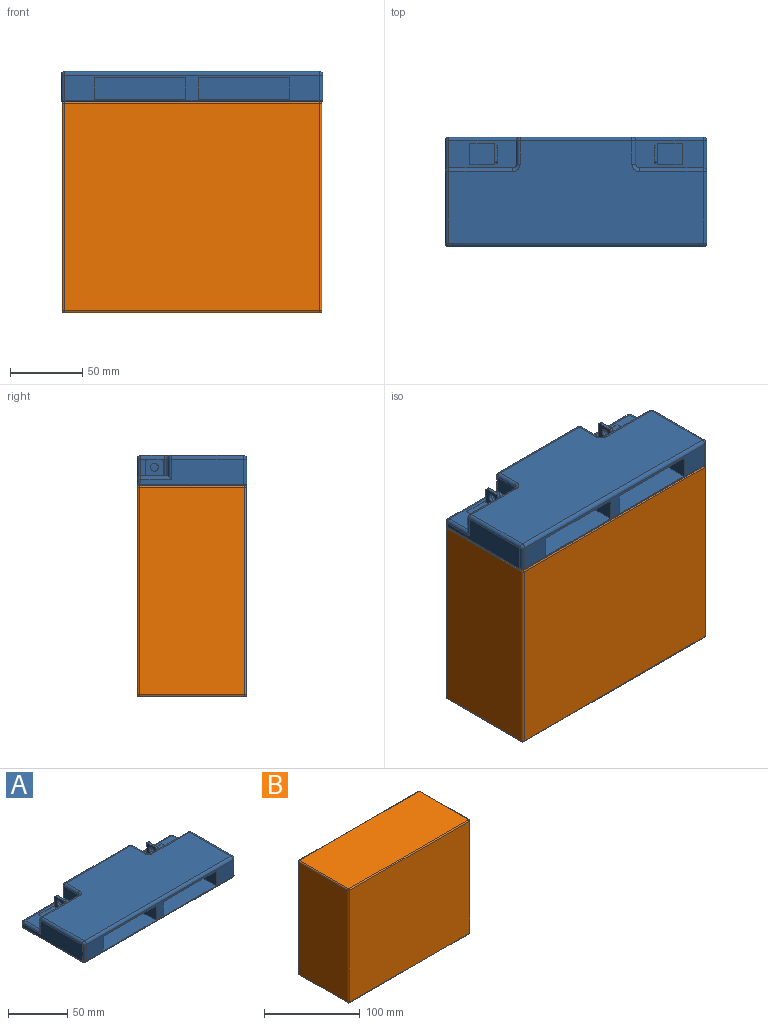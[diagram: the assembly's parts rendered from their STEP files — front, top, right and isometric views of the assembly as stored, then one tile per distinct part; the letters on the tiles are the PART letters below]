
ASSEMBLY  parts=2 mates=1
PART A: 104 faces, bbox 181.1x76x21.1 mm
  f0: plane 14.62x11.76mm, normal (-1,0,0), area 117.3mm2, adj f3,f4,f6,f7,f8,f9,f10,f61
  f1: plane 14.62x11.76mm, normal (1,0,0), area 117.3mm2, adj f11,f12,f13,f14,f21,f22,f65,f66
  f2: plane 179.61x74.45mm, normal (0,0,-1), area 13359mm2, adj f24,f25,f26,f27,f28,f29,f30,f31
  f3: cylinder r=1.27mm len=2.01mm, axis (1,0,0), area 4mm2, adj f0,f4,f5,f9
  f4: plane 9.45x2.01mm, normal (0,0,1), area 19mm2, adj f0,f3,f5,f6
  f5: plane 11.99x11.51mm, normal (1,0,0), area 113.6mm2, adj f3,f4,f6,f7,f8,f9,f10
  f6: cylinder r=1.27mm len=2.01mm, axis (1,0,0), area 4mm2, adj f0,f4,f5,f8
  f7: cylinder r=2.74mm len=5.49mm, axis (1,0,0), area 34.6mm2, adj f0,f5
  f8: plane 10.24x2.01mm, normal (0,1,0), area 20.5mm2, adj f0,f5,f6,f10
  f9: plane 10.24x2.01mm, normal (0,-1,0), area 20.5mm2, adj f0,f3,f5,f10
  f10: plane 46.74x18.8mm, normal (0,0,1), area 601.2mm2, adj f0,f5,f8,f9,f19,f60,f61,f62
  f11: cylinder r=1.27mm len=2.01mm, axis (-1,0,0), area 4mm2, adj f1,f12,f22,f23
  f12: plane 9.45x2.01mm, normal (0,0,1), area 19mm2, adj f1,f11,f13,f23
  f13: cylinder r=1.27mm len=2.01mm, axis (-1,0,0), area 4mm2, adj f1,f12,f21,f23
  f14: cylinder r=2.74mm len=5.49mm, axis (1,0,0), area 34.6mm2, adj f1,f23
  f15: plane 19.05x14.4mm, normal (-1,0,0), area 274.3mm2, adj f44,f45,f46,f71
  f16: plane 19.05x14.4mm, normal (1,0,0), area 274.3mm2, adj f44,f45,f46,f71
  f17: plane 19.05x14.4mm, normal (-1,0,0), area 274.3mm2, adj f47,f48,f49,f71
  f18: plane 19.05x14.4mm, normal (1,0,0), area 274.3mm2, adj f47,f48,f49,f71
  f19: plane 16.26x11.68mm, normal (-1,0,0), area 189.9mm2, adj f10,f86,f95,f96
  f20: plane 16.26x11.68mm, normal (1,0,0), area 189.9mm2, adj f79,f99,f101,f103
  f21: plane 10.24x2.01mm, normal (0,1,0), area 20.5mm2, adj f1,f13,f23,f99
  f22: plane 10.24x2.01mm, normal (0,-1,0), area 20.5mm2, adj f1,f11,f23,f99
  f23: plane 11.99x11.51mm, normal (-1,0,0), area 113.6mm2, adj f11,f12,f13,f14,f21,f22,f99
  f24: cylinder r=1.27mm len=174.5mm, axis (-1,0,0), area 256.9mm2, adj f2,f25,f26,f43
  f25: bspline ~1.22x0.92mm, area 1.3mm2, adj f2,f24,f27,f43
  f26: bspline ~1.22x0.92mm, area 1.3mm2, adj f2,f24,f28,f43
  f27: bspline ~2.54x2.54mm, area 5.7mm2, adj f2,f25,f29,f98
  f28: bspline ~2.54x2.54mm, area 5.7mm2, adj f2,f26,f30,f42
  f29: bspline ~1.22x0.92mm, area 1.3mm2, adj f2,f27,f31,f73
  f30: bspline ~1.22x0.92mm, area 1.3mm2, adj f2,f28,f32,f41
  f31: cylinder r=1.27mm len=69.34mm, axis (0,-1,0), area 102.1mm2, adj f2,f29,f33,f73
  f32: cylinder r=1.27mm len=69.34mm, axis (0,1,0), area 102.1mm2, adj f2,f30,f34,f41
  f33: bspline ~1.22x0.92mm, area 1.3mm2, adj f2,f31,f35,f73
  f34: bspline ~1.22x0.92mm, area 1.3mm2, adj f2,f32,f36,f41
  f35: bspline ~2.54x2.54mm, area 5.7mm2, adj f2,f33,f37,f72
  f36: bspline ~2.54x2.54mm, area 5.7mm2, adj f2,f34,f38,f40
  f37: bspline ~1.22x0.92mm, area 1.3mm2, adj f2,f35,f39,f71
  f38: bspline ~1.22x0.92mm, area 1.3mm2, adj f2,f36,f39,f71
  f39: cylinder r=1.27mm len=174.5mm, axis (1,0,0), area 256.9mm2, adj f2,f37,f38,f71
  f40: cylinder r=2.54mm len=3.1mm, axis (0,0,1), area 12.4mm2, adj f36,f41,f71,f76
  f41: plane 70.87x17.38mm, normal (-1,0,0), area 928mm2, adj f30,f32,f34,f40,f42,f74,f82,f93
  f42: cylinder r=2.54mm len=17.33mm, axis (0,0,1), area 69.1mm2, adj f28,f41,f43,f83
  f43: plane 176.02x17.38mm, normal (0,-1,0), area 1128.3mm2, adj f24,f25,f26,f42,f50,f51,f52,f53
  f44: plane 33.02x19.05mm, normal (0,0,1), area 629mm2, adj f15,f16,f46,f71
  f45: plane 33.02x19.05mm, normal (0,0,-1), area 629mm2, adj f15,f16,f46,f71
  f46: plane 33.02x14.4mm, normal (0,1,0), area 475.5mm2, adj f15,f16,f44,f45
  f47: plane 33.02x19.05mm, normal (0,0,1), area 629mm2, adj f17,f18,f49,f71
  f48: plane 33.02x19.05mm, normal (0,0,-1), area 629mm2, adj f17,f18,f49,f71
  f49: plane 33.02x14.4mm, normal (0,1,0), area 475.5mm2, adj f17,f18,f47,f48
  f50: plane 19.56x15.2mm, normal (1,0,0), area 297.3mm2, adj f43,f51,f53,f54
  f51: plane 63.5x19.56mm, normal (0,0,1), area 1241.9mm2, adj f43,f50,f52,f54
  f52: plane 19.56x15.2mm, normal (-1,0,0), area 297.3mm2, adj f43,f51,f53,f54
  f53: plane 63.5x19.56mm, normal (0,0,-1), area 1241.9mm2, adj f43,f50,f52,f54
  f54: plane 63.5x15.2mm, normal (0,-1,0), area 965.3mm2, adj f50,f51,f52,f53
  f55: plane 19.56x15.2mm, normal (1,0,0), area 297.3mm2, adj f43,f56,f58,f59
  f56: plane 63.5x19.56mm, normal (0,0,1), area 1241.9mm2, adj f43,f55,f57,f59
  f57: plane 19.56x15.2mm, normal (-1,0,0), area 297.3mm2, adj f43,f56,f58,f59
  f58: plane 63.5x19.56mm, normal (0,0,-1), area 1241.9mm2, adj f43,f55,f57,f59
  f59: plane 63.5x15.2mm, normal (0,-1,0), area 965.3mm2, adj f55,f56,f57,f58
  f60: plane 14.62x0.25mm, normal (1,0,0), area 3.7mm2, adj f10,f61,f62,f63
  f61: plane 17.22x0.25mm, normal (0,-1,0), area 4.4mm2, adj f0,f10,f60,f63
  f62: plane 17.22x0.25mm, normal (0,1,0), area 4.4mm2, adj f0,f10,f60,f63
  f63: plane 17.22x14.62mm, normal (0,0,1), area 251.8mm2, adj f0,f60,f61,f62
  f64: plane 14.62x0.25mm, normal (-1,0,0), area 3.7mm2, adj f65,f66,f67,f99
  f65: plane 17.22x0.25mm, normal (0,-1,0), area 4.4mm2, adj f1,f64,f67,f99
  f66: plane 17.22x0.25mm, normal (0,1,0), area 4.4mm2, adj f1,f64,f67,f99
  f67: plane 17.22x14.62mm, normal (0,0,1), area 251.8mm2, adj f1,f64,f65,f66
  f68: cylinder r=2.54mm len=49.28mm, axis (-1,0,0), area 191.5mm2, adj f70,f71,f99,f103
  f69: cylinder r=2.54mm len=21.34mm, axis (0,1,0), area 80.1mm2, adj f70,f73,f99,f100
  f70: sphere r=2.54mm, area 6.5mm2, adj f68,f69,f72
  f71: plane 176.02x17.38mm, normal (0,1,0), area 706.1mm2, adj f15,f16,f17,f18,f37,f38,f39,f40
  f72: cylinder r=2.54mm len=3.1mm, axis (0,0,1), area 12.4mm2, adj f35,f70,f71,f73
  f73: plane 70.87x17.38mm, normal (1,0,0), area 928mm2, adj f29,f31,f33,f69,f72,f80,f98,f100
  f74: cylinder r=2.54mm len=21.34mm, axis (0,-1,0), area 80.1mm2, adj f10,f41,f76,f93
  f75: cylinder r=2.54mm len=49.28mm, axis (-1,0,0), area 191.5mm2, adj f10,f71,f76,f96
  f76: sphere r=2.54mm, area 13.8mm2, adj f40,f74,f75
  f77: cylinder r=2.54mm len=44.2mm, axis (-1,0,0), area 176.3mm2, adj f78,f89,f97,f102
  f78: torus R=5.08mm, axis (0,0,1), area 21.7mm2, adj f77,f79,f97,f101
  f79: cylinder r=2.54mm len=16.26mm, axis (0,1,0), area 64.9mm2, adj f20,f78,f92,f97
  f80: cylinder r=2.54mm len=49.53mm, axis (0,-1,0), area 197.6mm2, adj f73,f88,f89,f97
  f81: cylinder r=2.54mm len=176.02mm, axis (-1,0,0), area 702.3mm2, adj f43,f83,f88,f97
  f82: cylinder r=2.54mm len=49.53mm, axis (0,1,0), area 197.6mm2, adj f41,f83,f87,f97
  f83: sphere r=2.54mm, area 10.1mm2, adj f42,f81,f82
  f84: cylinder r=2.54mm len=44.2mm, axis (-1,0,0), area 176.3mm2, adj f85,f87,f94,f97
  f85: torus R=5.08mm, axis (0,0,1), area 21.7mm2, adj f84,f86,f95,f97
  f86: cylinder r=2.54mm len=16.26mm, axis (0,-1,0), area 64.9mm2, adj f19,f85,f91,f97
  f87: sphere r=2.54mm, area 13.8mm2, adj f82,f84,f93
  f88: sphere r=2.54mm, area 10.1mm2, adj f80,f81,f98
  f89: sphere r=2.54mm, area 6.5mm2, adj f77,f80,f100
  f90: cylinder r=2.54mm len=77.47mm, axis (1,0,0), area 309.1mm2, adj f71,f91,f92,f97
  f91: sphere r=2.54mm, area 13.8mm2, adj f86,f90,f96
  f92: sphere r=2.54mm, area 6.5mm2, adj f79,f90,f103
  f93: cylinder r=2.54mm len=14.22mm, axis (0,0,-1), area 51.7mm2, adj f41,f74,f87,f94
  f94: plane 44.2x11.68mm, normal (0,1,0), area 516.4mm2, adj f10,f84,f93,f95
  f95: cylinder r=2.54mm len=11.68mm, axis (0,0,-1), area 46.6mm2, adj f10,f19,f85,f94
  f96: cylinder r=2.54mm len=14.22mm, axis (0,0,1), area 51.7mm2, adj f19,f71,f75,f91
  f97: plane 176.02x70.87mm, normal (0,0,1), area 10382.3mm2, adj f77,f78,f79,f80,f81,f82,f84,f85
  f98: cylinder r=2.54mm len=17.33mm, axis (0,0,1), area 69.1mm2, adj f27,f43,f73,f88
  f99: plane 46.74x18.8mm, normal (0,0,1), area 601.2mm2, adj f1,f20,f21,f22,f23,f64,f65,f66
  f100: cylinder r=2.54mm len=14.22mm, axis (0,0,1), area 51.7mm2, adj f69,f73,f89,f102
  f101: cylinder r=2.54mm len=11.68mm, axis (0,0,-1), area 46.6mm2, adj f20,f78,f99,f102
  f102: plane 44.2x11.68mm, normal (0,1,0), area 516.4mm2, adj f77,f99,f100,f101
  f103: cylinder r=2.54mm len=14.22mm, axis (0,0,-1), area 51.7mm2, adj f20,f68,f71,f92
PART B: 26 faces, bbox 179.6x75.4x145.8 mm
  f0: sphere r=1.27mm, area 2.5mm2, adj f3,f18,f19
  f1: sphere r=1.27mm, area 2.5mm2, adj f6,f9,f19
  f2: sphere r=1.27mm, area 2.5mm2, adj f3,f7,f16
  f3: cylinder r=1.27mm len=143.26mm, axis (0,0,1), area 285.8mm2, adj f0,f2,f20,f24
  f4: sphere r=1.27mm, area 2.5mm2, adj f11,f17,f18
  f5: sphere r=1.27mm, area 2.5mm2, adj f6,f7,f14
  f6: cylinder r=1.27mm len=143.26mm, axis (0,0,1), area 285.8mm2, adj f1,f5,f20,f21
  f7: cylinder r=1.27mm len=72.9mm, axis (0,1,0), area 145.4mm2, adj f2,f5,f20,f22
  f8: sphere r=1.27mm, area 2.5mm2, adj f9,f13,f17
  f9: cylinder r=1.27mm len=177.04mm, axis (1,0,0), area 353.2mm2, adj f1,f8,f21,f23
  f10: sphere r=1.27mm, area 2.5mm2, adj f11,f15,f16
  f11: cylinder r=1.27mm len=143.26mm, axis (0,0,1), area 285.8mm2, adj f4,f10,f24,f25
  f12: sphere r=1.27mm, area 2.5mm2, adj f13,f14,f15
  f13: cylinder r=1.27mm len=143.26mm, axis (0,0,1), area 285.8mm2, adj f8,f12,f21,f25
  f14: cylinder r=1.27mm len=177.04mm, axis (1,0,0), area 353.2mm2, adj f5,f12,f21,f22
  f15: cylinder r=1.27mm len=72.9mm, axis (0,-1,0), area 145.4mm2, adj f10,f12,f22,f25
  f16: cylinder r=1.27mm len=177.04mm, axis (-1,0,0), area 353.2mm2, adj f2,f10,f22,f24
  f17: cylinder r=1.27mm len=72.9mm, axis (0,-1,0), area 145.4mm2, adj f4,f8,f23,f25
  f18: cylinder r=1.27mm len=177.04mm, axis (-1,0,0), area 353.2mm2, adj f0,f4,f23,f24
  f19: cylinder r=1.27mm len=72.9mm, axis (0,1,0), area 145.4mm2, adj f0,f1,f20,f23
  f20: plane 143.26x72.9mm, normal (-1,0,0), area 10443.1mm2, adj f3,f6,f7,f19
  f21: plane 177.04x143.26mm, normal (0,1,0), area 25361.8mm2, adj f6,f9,f13,f14
  f22: plane 177.04x72.9mm, normal (0,0,1), area 12905.7mm2, adj f7,f14,f15,f16
  f23: plane 177.04x72.9mm, normal (0,0,-1), area 12905.7mm2, adj f9,f17,f18,f19
  f24: plane 177.04x143.26mm, normal (0,-1,0), area 25361.8mm2, adj f3,f11,f16,f18
  f25: plane 143.26x72.9mm, normal (1,0,0), area 10443.1mm2, adj f11,f13,f15,f17
PLACE A t=(-56.68,23.22,6.1)mm
PLACE B rot(axis=(0,1,0),180deg) t=(-56.68,23.22,145.8)mm
MATE fastened B.f23 <-> A.f2  axis (0,0,1) through (0,0,145.8)mm
